# Revit family: STS-108 Извещатель охранный_ПРД_RV17_LOD400
name_source: partatom
category: Датчики
revit_build: Autodesk Revit 2017 (Build: 20170118_1100(x64)
units: mm (PartAtom-declared; Revit-internal decimal feet)

## family parameters
Всегда вертикально = Нет
На основе рабочей плоскости = Нет
Общий = Нет
При загрузке вырезать с полостями = Нет
Размер круглого соединителя = Использовать диаметр
Сохранять ориентацию аннотаций = Нет
Тип детали = Нормальный
Точка расчета площади = Нет

## types (1)
- STS-108 Извещатель охранный (Передатчик)
    ADSK_URL страницы изделия = https://stilsoft.ru
    ADSK_Единица измерения = шт.
    ADSK_Завод-изготовитель = ООО «Основа Безопасности»
    ADSK_Количество = 1
    ADSK_Марка = СТВФ.426479.006
    ADSK_Масса = 2
    ADSK_Наименование = Извещатель охранный STS-107
    ADSK_Размер_Высота = 141 мм
    ADSK_Размер_Длина = 210 мм
    ADSK_Размер_Ширина = 210 мм
    d_короба = 20 мм
    Вероятность обнаружения при доверительной вероятности 0,9, не менее = 0.98
    Время восстановления дежурного режима, не более, с = 10
    Время технической готовности после включения питания, не более, с = 30
    Диапазон обнаруживаемых скоростей, м/с = от 0,1 до 10,0
    Диапазон рабочих температур, °С = от -50 до +70
    Длительность извещения, не менее, с = 3
    Информационный выход = релейный
    Максимальная высота зоны обнаружения от места установки, м = 1.5
    Максимальная высота неровностей земли, снежного и травяного покрова, м = 1
    Максимальная ширина зоны обнаружения, м = 4
    Напряжение электропитания постоянного тока, В = от 10,2 до 36
    Период наработки на ложное срабатывание, не менее, ч = 1200
    Потребляемый ток при напряжении питания 12 В, не более, мА = 50
    Протяженность зоны обнаружения, м = от 5 до 200
    Рабочая частота, ГГц = 10,55
    Режим работы = круглосуточный
